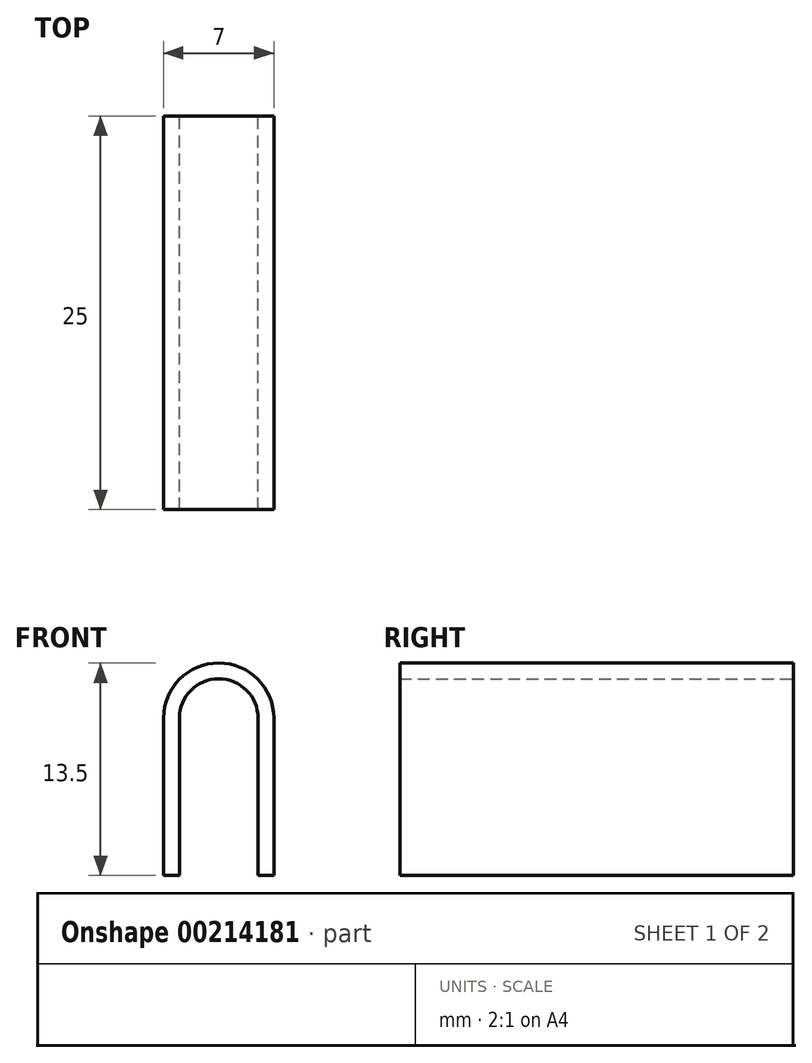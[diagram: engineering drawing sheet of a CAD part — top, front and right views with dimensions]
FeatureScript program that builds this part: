
annotation { "Feature Type Name" : "Feature", "Feature Type Description" : "" }
export const myFeature = defineFeature(function(context is Context, id is Id, definition is map)
    precondition{}
    {
        {
            var Q0;
            Q0=qCreatedBy(makeId("Front.planeOp"),FACE);
            var sketch = newSketch(context, id + "F0", { "sketchPlane" : qUnion([Q0])});
            skArc(sketch, "E0", {"start": v(1.55, 0) * mm, "mid": v(-0.95, 2.5) * mm, "end": v(-3.45, 0) * mm});
            skLineSegment(sketch, "E1", {"start": v(-3.45, 0) * mm, "end": v(-3.45, -10) * mm});
            skLineSegment(sketch, "E2", {"start": v(1.55, 0) * mm, "end": v(1.55, -10) * mm});
            skLineSegment(sketch, "E3.0", {"start": v(-4.45, 0) * mm, "end": v(-4.45, -10) * mm});
            skArc(sketch, "E3.1", {"start": v(2.55, 0) * mm, "mid": v(-0.95, 3.5) * mm, "end": v(-4.45, 0) * mm});
            skLineSegment(sketch, "E3.2", {"start": v(2.55, 0) * mm, "end": v(2.55, -10) * mm});
            skLineSegment(sketch, "E4", {"start": v(-4.45, -10) * mm, "end": v(-3.45, -10) * mm});
            skLineSegment(sketch, "E5", {"start": v(1.55, -10) * mm, "end": v(2.55, -10) * mm});
            skSolve(sketch);
        }
        {
            var Q0;
            Q0 = qSketchRegion(id + "F0", true);
            extrude(context, id + "F1", {"entities" : qUnion([Q0]), "depth" : 25 * mm});
        }
    });
